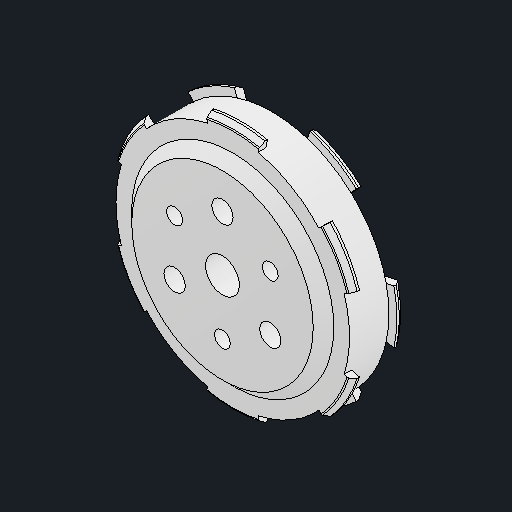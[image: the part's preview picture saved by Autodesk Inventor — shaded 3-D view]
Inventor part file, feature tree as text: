
AUTODESK INVENTOR PART (.ipt)
format: ipt  version: 2023.2 (Build 272271030, 271C)  size: 435,712 bytes
history: native  units: mm
features: sketch x15, extrude x13, chamfer x3, pattern_circular x3, projected_geometry x3, other x2, fillet x2, plane x1, revolve x1
ambient origin geometry x8: Origin, YZ Plane, XZ Plane, XY Plane, X Axis, Y Axis, Z Axis, Center Point
bodies: Body1 (feature_tree)
feature tree (43):
  other  "ソリッド1"
  extrude  "押し出し1"  Depth=0.5mm TaperAngle=0.0deg
  extrude  "押し出し2"  Depth=0.5mm
  sketch  "スケッチ3"
  plane  "Work Plane2"
  revolve  "回転2"
  chamfer  "面取り1"  Distance=1.3mm
  chamfer  "面取り2"  Distance=26.0mm
  extrude  "押し出し4"  Depth=1.0mm
  extrude  "押し出し5"  Depth=1.0mm
  pattern_circular  "Circular Pattern6"  [2 undecoded]
  extrude  "押し出し6"  TaperAngle=90.0deg  [1 undecoded]
  extrude  "押し出し7"  Depth=0.5mm TaperAngle=45.0deg
  extrude  "押し出し9"  Depth=0.5mm TaperAngle=45.0deg
  extrude  "押し出し10"  Depth=0.5mm
  extrude  "押し出し11"  Depth=0.5mm
  extrude  "押し出し12"  TaperAngle=150.0deg  [1 undecoded]
  extrude  "押し出し13"  Depth=1.3mm TaperAngle=0.0deg
  pattern_circular  "円形状パターン5"  [2 undecoded]
  sketch  "スケッチ18"
  other  "作業平面1"
  extrude  "押し出し14"  Depth=0.5mm
  fillet  "フィレット1"  Radius=1.3mm
  fillet  "フィレット3"  Radius=4.5mm
  chamfer  "Chamfer3"  Distance=1.3mm
  extrude  "Extrusion15"  Depth=7.0mm
  pattern_circular  "Circular Pattern7"  [2 undecoded]
  sketch  "スケッチ1"
  sketch  "スケッチ2"
  sketch  "スケッチ6"
  sketch  "スケッチ7"
  sketch  "スケッチ8"
  sketch  "スケッチ10"
  sketch  "スケッチ13"
  sketch  "スケッチ14"
  sketch  "スケッチ15"
  sketch  "スケッチ16"
  sketch  "スケッチ17"
  sketch  "スケッチ19"
  projected_geometry  "Projected Loop3"
  projected_geometry  "Projected Loop4"
  sketch  "Sketch20"  dims[d0=31.6mm d1=7.3mm d2=0.0mm d3=3.0mm d4=1.3mm d5=0.0mm d6=26.0mm d18=1.0mm d19=1.0mm d20=1.0mm d21=90.0deg d22=0.7mm d23=0.5mm d24=45.0deg d25=0.7mm d26=0.5mm d27=45.0deg d28=5.0mm d29=5.0mm d30=150.0deg d31=1.3mm d32=0.0mm d36=5.0mm d37=5.0mm d38=1.3mm d39=0.0mm d43=4.5mm d44=0.0mm d45=1.3mm d46=0.0mm d53=7.0mm d54=5.0mm d55=7.0mm d56=30.0mm d58=360.0deg d60=5.8mm d61=0.0mm d62=7.0mm d63=7.0mm d64=0.0mm d65=2.7mm d66=0.0mm d67=0.0mm d71=4.3mm d72=0.0mm d73=0.0mm d74=7.0mm d75=2.0mm d76=0.0mm d77=0.0mm d78=30.0mm d79=360.0deg d81=1.0mm d82=1.0mm d83=3.0mm d84=7.0mm d85=0.0mm d86=0.2mm d88=0.2mm d93=25.6mm d94=30.0deg d95=60.0mm d96=360.0deg d98=1.3mm d99=2.0mm d100=45.0deg d101=1.3mm d102=0.5mm d103=0.0mm d104=30.0mm d105=360.0deg d33=0.5mm d34=0.872665mm d107=0.5mm d108=0.872665mm d109=0.5mm d110=0.872665mm]
  projected_geometry  "Projected Loop5"
note: 8 required parameter values undecoded (feature->parameter linkage not recoverable at this tier; creation-order binding heuristic only, values carry confidence <= 0.55)
